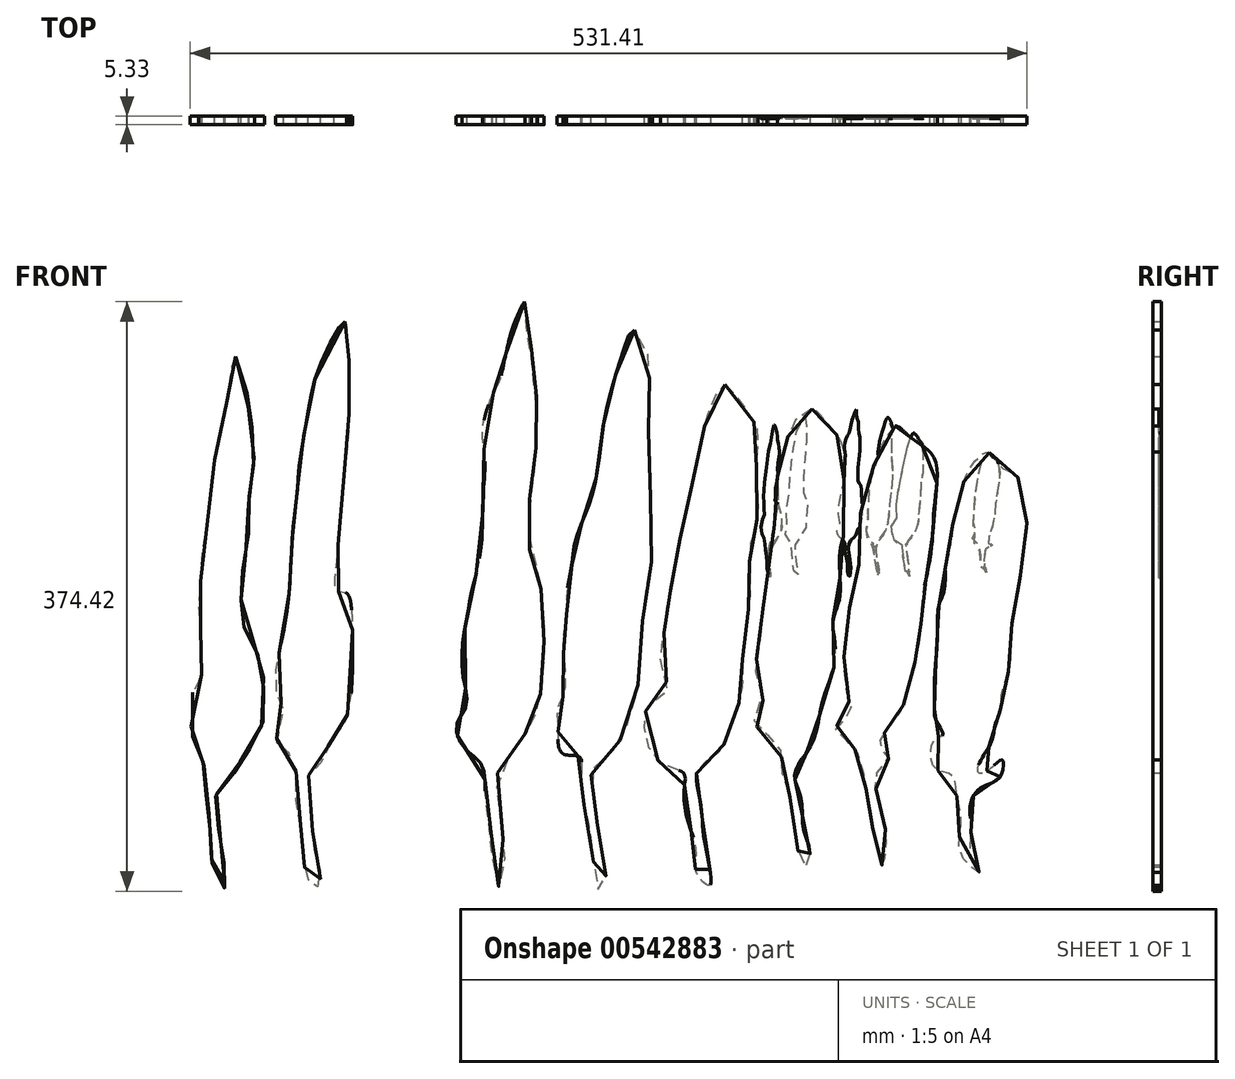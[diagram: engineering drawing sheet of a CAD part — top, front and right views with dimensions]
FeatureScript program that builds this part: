
annotation { "Feature Type Name" : "Feature", "Feature Type Description" : "" }
export const myFeature = defineFeature(function(context is Context, id is Id, definition is map)
    precondition{}
    {
        {
            var Q0;
            Q0=qCreatedBy(makeId("Front.planeOp"),FACE);
            var sketch = newSketch(context, id + "F0", { "sketchPlane" : qUnion([Q0])});
            skFitSpline(sketch, "E0", {"points": [v(-26.75, 46.41) * mm, v(-26.5, 43.12) * mm, v(-26, 39.07) * mm, v(-26, 32.23) * mm, v(-26.25, 24.64) * mm, v(-27.51, 13) * mm, v(-28.33, 2.5) * mm, v(-28.33, -2.36) * mm, v(-26.56, -2.8) * mm, v(-25.46, -7.65) * mm, v(-26.25, -24.73) * mm, v(-28.52, -28.78) * mm, v(-29.8, -30.55) * mm, v(-30.55, -33.08) * mm, v(-33.08, -35.36) * mm, v(-32.83, -41.7) * mm, v(-32.32, -49.5) * mm, v(-31.2, -54.37) * mm, v(-32.07, -56.37) * mm, v(-33.62, -54.37) * mm, v(-34.3, -49.5) * mm, v(-34.72, -45.33) * mm, v(-35.61, -40.17) * mm, v(-36.26, -32.55) * mm, v(-38.9, -30.55) * mm, v(-38.46, -26.6) * mm, v(-37.9, -23.97) * mm, v(-39.16, -20.94) * mm, v(-38.69, -13.6) * mm, v(-37.14, -5.44) * mm, v(-36.48, 4.03) * mm, v(-36.04, 9.98) * mm, v(-35.38, 15.94) * mm, v(-34.94, 21.22) * mm, v(-33.59, 29.2) * mm, v(-31.56, 37.8) * mm, v(-26.75, 46.41) * mm]});
            skFitSpline(sketch, "E1", {"points": [v(-8.5, 48.51) * mm, v(-7.65, 45.54) * mm, v(-7.65, 41.3) * mm, v(-7.65, 37.26) * mm, v(-7.86, 34.07) * mm, v(-8.29, 28.97) * mm, v(-8.71, 24.09) * mm, v(-9.35, 21.33) * mm, v(-9.14, 17.5) * mm, v(-9.77, 12.62) * mm, v(-8.71, 6.89) * mm, v(-7.65, 3.27) * mm, v(-7.44, -2.25) * mm, v(-6.8, -4.8) * mm, v(-6.8, -7.77) * mm, v(-7.22, -10.32) * mm, v(-7.86, -15) * mm, v(-8.29, -19.66) * mm, v(-9.99, -23.7) * mm, v(-11.47, -26.67) * mm, v(-12.32, -29.64) * mm, v(-15.08, -31.98) * mm, v(-16.14, -33.9) * mm, v(-16.14, -38.14) * mm, v(-15.72, -43.24) * mm, v(-15.08, -45.79) * mm, v(-14.45, -50.03) * mm, v(-14.02, -54.7) * mm, v(-14.66, -56.2) * mm, v(-15.72, -54.7) * mm, v(-16.36, -52.16) * mm, v(-16.78, -48.76) * mm, v(-17.63, -44.72) * mm, v(-18.06, -40.05) * mm, v(-18.48, -35.6) * mm, v(-19.33, -33.47) * mm, v(-22.1, -32.4) * mm, v(-23.58, -29.64) * mm, v(-23.15, -27.1) * mm, v(-22.1, -23.91) * mm, v(-22.1, -23.91) * mm, v(-21.24, -20.94) * mm, v(-22.1, -18.39) * mm, v(-22.73, -14.57) * mm, v(-22.73, -10.53) * mm, v(-22.1, -7.56) * mm, v(-21.67, -4.37) * mm, v(-21.45, 0) * mm, v(-21.03, 2.85) * mm, v(-20.18, 5.19) * mm, v(-18.48, 7.52) * mm, v(-18.48, 11.35) * mm, v(-17.84, 17.08) * mm, v(-17.2, 22.39) * mm, v(-16.57, 27.27) * mm, v(-15.72, 31.73) * mm, v(-14.87, 35.56) * mm, v(-13.6, 41.08) * mm, v(-11.68, 43.63) * mm, v(-10.4, 46.39) * mm, v(-8.5, 48.51) * mm]});
            skFitSpline(sketch, "E2", {"points": [v(-46.56, 40.04) * mm, v(-47.72, 35.4) * mm, v(-48.19, 31.7) * mm, v(-49.35, 26.59) * mm, v(-50.74, 18.7) * mm, v(-51.43, 11.74) * mm, v(-52.6, 5.25) * mm, v(-53.06, -1.94) * mm, v(-53.29, -5.88) * mm, v(-52.83, -10.3) * mm, v(-52.83, -14.47) * mm, v(-52.83, -17.95) * mm, v(-54.45, -21.2) * mm, v(-54.45, -28.59) * mm, v(-53.75, -30.24) * mm, v(-52.36, -33.95) * mm, v(-52.13, -37.66) * mm, v(-51.43, -42.53) * mm, v(-51.2, -46.47) * mm, v(-50.97, -50.65) * mm, v(-50.04, -54.82) * mm, v(-48.65, -56.45) * mm, v(-48.65, -54.13) * mm, v(-48.65, -51.58) * mm, v(-49.35, -47.63) * mm, v(-50.04, -43) * mm, v(-50.04, -39.28) * mm, v(-47.26, -36.5) * mm, v(-46.56, -34.65) * mm, v(-44.48, -31.86) * mm, v(-43.08, -29.08) * mm, v(-41.46, -25.83) * mm, v(-41.46, -21.89) * mm, v(-41.7, -16.55) * mm, v(-42.85, -13.07) * mm, v(-44.24, -9.6) * mm, v(-45.87, -8.44) * mm, v(-45.64, -4.72) * mm, v(-45.64, -1.7) * mm, v(-45.17, 2.23) * mm, v(-44.24, 7.57) * mm, v(-44.24, 11.98) * mm, v(-43.78, 17.77) * mm, v(-43.32, 20.33) * mm, v(-43.32, 25.43) * mm, v(-44.24, 30.53) * mm, v(-44.7, 35.17) * mm, v(-46.56, 40.04) * mm]});
            skFitSpline(sketch, "E3", {"points": [v(5.86, 50.01) * mm, v(5.86, 46.07) * mm, v(7.02, 42.13) * mm, v(7.02, 39.58) * mm, v(7.25, 35.87) * mm, v(8.18, 31.46) * mm, v(7.94, 27.52) * mm, v(7.94, 22.88) * mm, v(7.48, 18.47) * mm, v(6.78, 14.3) * mm, v(6.78, 9.89) * mm, v(6.78, 5.71) * mm, v(7.02, 3.63) * mm, v(8.4, 2.23) * mm, v(8.87, -2.4) * mm, v(9.33, -7.28) * mm, v(9.33, -11.22) * mm, v(9.33, -16.55) * mm, v(8.87, -20.03) * mm, v(7.94, -24.67) * mm, v(6.55, -26.3) * mm, v(5.86, -28.85) * mm, v(4.26, -31.3) * mm, v(1.32, -34.23) * mm, v(1.32, -43.58) * mm, v(1.94, -47.7) * mm, v(2.19, -52.4) * mm, v(1.32, -56.2) * mm, v(0, -52.4) * mm, v(0, -47.73) * mm, v(-1.22, -41.85) * mm, v(-1.35, -38.4) * mm, v(-1.95, -33.98) * mm, v(-5.05, -31) * mm, v(-6.5, -26.7) * mm, v(-4.8, -23.57) * mm, v(-5.22, -18.4) * mm, v(-5.45, -12.36) * mm, v(-4.55, -6.99) * mm, v(-3.66, -2.06) * mm, v(-2.54, 2.19) * mm, v(-1.87, 7.78) * mm, v(-1.62, 15.25) * mm, v(-1.37, 22.42) * mm, v(-1.8, 26.67) * mm, v(0, 33.06) * mm, v(1.32, 35.66) * mm, v(1.71, 37.09) * mm, v(2.38, 40.22) * mm, v(3.5, 44.7) * mm, v(5.86, 50.01) * mm]});
            skFitSpline(sketch, "E4", {"points": [v(-62.57, -56) * mm, v(-62.87, -50.88) * mm, v(-63.77, -44.86) * mm, v(-64.98, -39.44) * mm, v(-65.88, -34.31) * mm, v(-66.18, -27.38) * mm, v(-66.78, -19.55) * mm, v(-66.48, -14.73) * mm, v(-66.18, -8.1) * mm, v(-65.58, -2.37) * mm, v(-64.67, 3.95) * mm, v(-63.47, 10.58) * mm, v(-62.26, 15.1) * mm, v(-60.46, 18.72) * mm, v(-59.25, 15.1) * mm, v(-58.65, 10.28) * mm, v(-58.35, 2.75) * mm, v(-58.95, -3.28) * mm, v(-59.25, -10.2) * mm, v(-59.25, -15.63) * mm, v(-59.85, -19.55) * mm, v(-57.74, -24.37) * mm, v(-57.74, -28.59) * mm, v(-57.74, -28.59) * mm, v(-57.14, -34.31) * mm, v(-59.85, -38.83) * mm, v(-61.96, -42.75) * mm, v(-61.06, -51.19) * mm, v(-62.57, -56) * mm]});
            skFitSpline(sketch, "E5", {"points": [v(25.76, 44.9) * mm, v(23.67, 40.98) * mm, v(22.1, 35.74) * mm, v(20.52, 29.72) * mm, v(19.74, 24.48) * mm, v(18.95, 18.72) * mm, v(17.64, 13.49) * mm, v(16.07, 9.56) * mm, v(14.76, 5.37) * mm, v(14.5, 2.75) * mm, v(13.45, -3.27) * mm, v(13.45, -7.2) * mm, v(12.93, -10.34) * mm, v(12.93, -13.49) * mm, v(13.2, -17.94) * mm, v(12.93, -21.34) * mm, v(11.88, -23.44) * mm, v(11.88, -26.58) * mm, v(11.88, -29.46) * mm, v(12.93, -32.08) * mm, v(15.8, -32.6) * mm, v(16.07, -37.31) * mm, v(17.12, -43.34) * mm, v(18.17, -49.62) * mm, v(19.48, -56.95) * mm, v(20.52, -54.86) * mm, v(20, -50.4) * mm, v(18.95, -44.12) * mm, v(18.17, -38.1) * mm, v(18.17, -34.96) * mm, v(21.3, -32.08) * mm, v(24.19, -27.36) * mm, v(26.28, -20.3) * mm, v(27.07, -10.87) * mm, v(27.6, -4.58) * mm, v(28.9, 3.27) * mm, v(28.9, 10.87) * mm, v(28.38, 22.13) * mm, v(28.38, 28.67) * mm, v(28.38, 34.7) * mm, v(28.38, 39.93) * mm, v(25.76, 44.9) * mm]});
            skFitSpline(sketch, "E6", {"points": [v(42.26, 34.96) * mm, v(45.14, 31.55) * mm, v(48.02, 27.1) * mm, v(48.02, 23.17) * mm, v(48.02, 16.1) * mm, v(48.02, 10.34) * mm, v(46.7, 5.37) * mm, v(46.7, 2.23) * mm, v(46.7, -3.54) * mm, v(46.19, -7.72) * mm, v(45.4, -14.27) * mm, v(45.4, -18.98) * mm, v(44.61, -23.17) * mm, v(43.57, -26.32) * mm, v(41.2, -31.55) * mm, v(37.8, -34.17) * mm, v(37.02, -36.27) * mm, v(37.8, -41.24) * mm, v(38.33, -46.74) * mm, v(39.38, -52.5) * mm, v(39.38, -55.9) * mm, v(37.02, -53.55) * mm, v(37.02, -50.4) * mm, v(36.23, -46.48) * mm, v(34.93, -41.77) * mm, v(34.93, -37.31) * mm, v(34.66, -35.48) * mm, v(29.95, -33.12) * mm, v(27.6, -26.84) * mm, v(28.64, -22.91) * mm, v(31.78, -20.56) * mm, v(30.74, -16.63) * mm, v(31, -10.87) * mm, v(31.78, -5.1) * mm, v(32.3, -2.49) * mm, v(33.35, 3.27) * mm, v(34.66, 9.82) * mm, v(36.23, 16.89) * mm, v(38.07, 25.53) * mm, v(39.64, 31.03) * mm, v(42.26, 34.96) * mm]});
            skFitSpline(sketch, "E7", {"points": [v(90.18, 22.65) * mm, v(92.27, 20.03) * mm, v(95.15, 18.46) * mm, v(95.94, 14.8) * mm, v(96.99, 9.56) * mm, v(96.2, 3.54) * mm, v(95.41, -2.75) * mm, v(94.37, -7.72) * mm, v(94.1, -11.4) * mm, v(93.58, -17.41) * mm, v(92.27, -21.34) * mm, v(92.27, -23.7) * mm, v(91.22, -26.84) * mm, v(90.7, -29.46) * mm, v(88.08, -34.43) * mm, v(88.34, -35.48) * mm, v(90.7, -34.43) * mm, v(92.53, -33.12) * mm, v(92.27, -36) * mm, v(89.92, -37.58) * mm, v(88.08, -38.62) * mm, v(86.77, -40.98) * mm, v(86.77, -44.12) * mm, v(86.77, -47) * mm, v(87.03, -51.45) * mm, v(88.34, -53.55) * mm, v(85.17, -50.6) * mm, v(84.94, -45.96) * mm, v(84.94, -42.45) * mm, v(84.15, -38.62) * mm, v(83.63, -36) * mm, v(80.75, -34.96) * mm, v(79.44, -32.08) * mm, v(80.75, -28.94) * mm, v(81.8, -28.67) * mm, v(80.49, -25.8) * mm, v(80.23, -23.2) * mm, v(80.23, -17.94) * mm, v(80.75, -11.91) * mm, v(81.01, -5.1) * mm, v(82.06, -2.23) * mm, v(82.32, 2.49) * mm, v(83.37, 6.68) * mm, v(83.63, 9.82) * mm, v(84.68, 13.75) * mm, v(85.73, 17.94) * mm, v(88.08, 21.6) * mm, v(90.18, 22.65) * mm]});
            skFitSpline(sketch, "E8", {"points": [v(57.98, 30.54) * mm, v(54.5, 27.83) * mm, v(53.34, 23.96) * mm, v(51.8, 18.55) * mm, v(51.8, 12.37) * mm, v(49.86, 4.25) * mm, v(50.25, 1.93) * mm, v(49.47, -2.32) * mm, v(48.7, -10.44) * mm, v(47.93, -18.55) * mm, v(49.09, -22.42) * mm, v(47.93, -23.58) * mm, v(47.93, -27.06) * mm, v(51.8, -30.15) * mm, v(52.57, -35.56) * mm, v(54.11, -40.2) * mm, v(55.27, -49.09) * mm, v(57.2, -52.57) * mm, v(57.6, -49.47) * mm, v(56.43, -45.6) * mm, v(56.04, -40.2) * mm, v(54.88, -36.72) * mm, v(55.27, -34.4) * mm, v(56.82, -32.08) * mm, v(58.75, -28.22) * mm, v(59.9, -22.42) * mm, v(62.23, -14.69) * mm, v(61.84, -7.72) * mm, v(63, -3.87) * mm, v(63, 3.87) * mm, v(63.77, 8.5) * mm, v(63.77, 17.78) * mm, v(63.39, 24.35) * mm, v(59.9, 28.99) * mm, v(57.98, 30.54) * mm]});
            skFitSpline(sketch, "E9", {"points": [v(73.05, 27.44) * mm, v(69.57, 21.26) * mm, v(66.87, 11.98) * mm, v(66.48, 2.32) * mm, v(64.93, -5.02) * mm, v(63.77, -13.91) * mm, v(64.55, -22.03) * mm, v(64.93, -24.74) * mm, v(62.23, -27.44) * mm, v(64.93, -30.15) * mm, v(67.25, -35.17) * mm, v(68.41, -42.13) * mm, v(69.57, -48.32) * mm, v(70.73, -52.18) * mm, v(71.5, -47.54) * mm, v(70.35, -41.74) * mm, v(69.96, -35.17) * mm, v(71.9, -32.85) * mm, v(70.35, -30.54) * mm, v(72.66, -26.28) * mm, v(74.6, -23.2) * mm, v(76.53, -16.23) * mm, v(77.69, -10.44) * mm, v(78.08, -3.87) * mm, v(79.62, 4.64) * mm, v(80.23, 13.14) * mm, v(80.23, 21.65) * mm, v(75.76, 25.51) * mm, v(73.05, 27.44) * mm]});
            skSolve(sketch);
        }
        {
            var Q0;
            Q0 = qSketchRegion(id + "F0", true);
            extrude(context, id + "F1", {"entities" : qUnion([Q0]), "depth" : 1.52 * mm, "offsetDistance" : 25.4 * mm});
        }
        {
            var Q0;
            Q0=makeQuery(id+"F1.opExtrude","SWEPT_BODY",BODY,{"disambiguationData":[OSD([sQuery(id+"F0.wireOp",EDGE,"E4")])]});
            var Q1;
            Q1=makeQuery(id+"F1.opExtrude","SWEPT_BODY",BODY,{"disambiguationData":[OSD([sQuery(id+"F0.wireOp",EDGE,"E2")])]});
            var Q2;
            Q2=makeQuery(id+"F1.opExtrude","SWEPT_BODY",BODY,{"disambiguationData":[OSD([sQuery(id+"F0.wireOp",EDGE,"E1")])]});
            var Q3;
            Q3=makeQuery(id+"F1.opExtrude","SWEPT_BODY",BODY,{"disambiguationData":[OSD([sQuery(id+"F0.wireOp",EDGE,"E0")])]});
            var Q4;
            Q4=makeQuery(id+"F1.opExtrude","SWEPT_BODY",BODY,{"disambiguationData":[OSD([sQuery(id+"F0.wireOp",EDGE,"E3")])]});
            var Q5;
            Q5=makeQuery(id+"F1.opExtrude","SWEPT_BODY",BODY,{"disambiguationData":[OSD([sQuery(id+"F0.wireOp",EDGE,"E5")])]});
            var Q6;
            Q6=makeQuery(id+"F1.opExtrude","SWEPT_BODY",BODY,{"disambiguationData":[OSD([sQuery(id+"F0.wireOp",EDGE,"E6")])]});
            var Q7;
            Q7=makeQuery(id+"F1.opExtrude","SWEPT_BODY",BODY,{"disambiguationData":[OSD([sQuery(id+"F0.wireOp",EDGE,"E8")])]});
            var Q8;
            Q8=makeQuery(id+"F1.opExtrude","SWEPT_BODY",BODY,{"disambiguationData":[OSD([sQuery(id+"F0.wireOp",EDGE,"E9")])]});
            var Q9;
            Q9=makeQuery(id+"F1.opExtrude","SWEPT_BODY",BODY,{"disambiguationData":[OSD([sQuery(id+"F0.wireOp",EDGE,"E7")])]});
            var Q10;
            Q10=sQuery(id+"F0.wireOp",VERTEX,"E7.0.internal");
            transform(context, id + "F2", {"entities" : qUnion([Q0, Q1, Q2, Q3, Q4, Q5, Q6, Q7, Q8, Q9]), "transformType" : TransformType.SCALE_UNIFORMLY, "scale" : 3.5, "scalePoint" : qUnion([Q10]), "makeCopy" : false});
        }
        {
            var Q0;
            Q0=makeQuery(id+"F1.opExtrude","CAP_FACE",FACE,{"disambiguationData":[OSD([sQuery(id+"F0.wireOp",EDGE,"E4")])],"isStart":false});
            var sketch = newSketch(context, id + "F3", { "sketchPlane" : qUnion([Q0])});
            skPoint(sketch, "E10", {"position": v(87.01, 21.31) * mm});
            skPoint(sketch, "E11", {"position": v(82.1, -244.62) * mm});
            skPoint(sketch, "E12", {"position": v(64.9, -40.1) * mm});
            skPoint(sketch, "E13", {"position": v(112.8, -26.6) * mm});
            skSolve(sketch);
        }
        {
            var Q0;
            Q0=makeQuery(id+"F0.imprint","IMPRINT",FACE,{"disambiguationData":[TD([[makeQuery(id+"F0.imprint","IMPRINT",EDGE,{"derivedFrom":sQuery(id+"F0.wireOp",EDGE,"E4")}),-1.0]])]});
            var Q1;
            Q1=makeQuery(id+"F0.imprint","IMPRINT",FACE,{"disambiguationData":[TD([[makeQuery(id+"F0.imprint","IMPRINT",EDGE,{"derivedFrom":sQuery(id+"F0.wireOp",EDGE,"E2")}),1.0]])]});
            var Q2;
            Q2=makeQuery(id+"F0.imprint","IMPRINT",FACE,{"disambiguationData":[TD([[makeQuery(id+"F0.imprint","IMPRINT",EDGE,{"derivedFrom":sQuery(id+"F0.wireOp",EDGE,"E0")}),-1.0]])]});
            var Q3;
            Q3=makeQuery(id+"F0.imprint","IMPRINT",FACE,{"disambiguationData":[TD([[makeQuery(id+"F0.imprint","IMPRINT",EDGE,{"derivedFrom":sQuery(id+"F0.wireOp",EDGE,"E1")}),-1.0]])]});
            var Q4;
            Q4=makeQuery(id+"F0.imprint","IMPRINT",FACE,{"disambiguationData":[TD([[makeQuery(id+"F0.imprint","IMPRINT",EDGE,{"derivedFrom":sQuery(id+"F0.wireOp",EDGE,"E3")}),-1.0]])]});
            var Q5;
            Q5=makeQuery(id+"F0.imprint","IMPRINT",FACE,{"disambiguationData":[TD([[makeQuery(id+"F0.imprint","IMPRINT",EDGE,{"derivedFrom":sQuery(id+"F0.wireOp",EDGE,"E5")}),1.0]])]});
            var Q6;
            Q6=makeQuery(id+"F0.imprint","IMPRINT",FACE,{"disambiguationData":[TD([[makeQuery(id+"F0.imprint","IMPRINT",EDGE,{"derivedFrom":sQuery(id+"F0.wireOp",EDGE,"E6")}),-1.0]])]});
            var Q7;
            Q7=makeQuery(id+"F0.imprint","IMPRINT",FACE,{"disambiguationData":[TD([[makeQuery(id+"F0.imprint","IMPRINT",EDGE,{"derivedFrom":sQuery(id+"F0.wireOp",EDGE,"E7")}),-1.0]])]});
            extrude(context, id + "F4", {"entities" : qUnion([Q0, Q1, Q2, Q3, Q4, Q5, Q6, Q7]), "depth" : 1.52 * mm, "offsetDistance" : 25.4 * mm});
        }
    });
